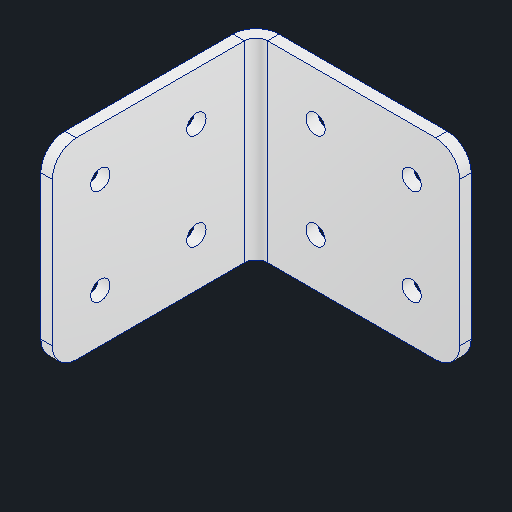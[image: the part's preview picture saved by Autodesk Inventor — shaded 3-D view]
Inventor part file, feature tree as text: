
AUTODESK INVENTOR PART (.ipt)
format: ipt  version: 2024.3 (Build 283343010, 343A)  size: 188,928 bytes
history: native  units: in
note: dims shown in document units (in); Inventor stores cm internally (conversion verified against a paired STEP export)
features: sheet_metal_op x4, sketch x4, hole x2, other x2, projected_geometry x2, chamfer x1
ambient origin geometry x8: Origin, YZ Plane, XZ Plane, XY Plane, X Axis, Y Axis, Z Axis, Center Point
bodies: Solid1 (feature_tree)
feature tree (15):
  sheet_metal_op  "Face1"
  sheet_metal_op  "Flange1"
  hole  "Hole1"  [1 undecoded]
  hole  "Hole2"  [1 undecoded]
  chamfer  "Corner Round1"
  sketch  "Sketch1"  dims[d0=2.0in d1=2.0in]
  other  "Plate1"
  sketch  "Sketch2"  dims[d2=0.12in d3=0.12in]
  other  "Plate2"
  sheet_metal_op  "Bend1"
  sheet_metal_op  "Corner1"
  sketch  "Sketch3"  dims[d4=0.06in]
  projected_geometry  "Projected Loop1"
  sketch  "Sketch4"  dims[d5=0.24in d6=0.12in d7=2.24in d8=90.0deg d9=0.12in d10=0.48in d11=0.12in d12=0.12in d13=0.5in d14=0.5in d15=0.7874in d17=1.0in d18=0.7874in d20=1.0in d23=0.201in d24=0.75in d25=0.385in d26=0.25in d27=0.5635in d28=0.12in d29=0.8108in d30=0.5in d31=0.5in d32=0.7874in d34=1.0in d35=0.7874in d37=1.0in d40=0.201in d41=0.75in d42=0.375in d43=0.25in d44=0.5635in d45=1.0in d46=0.8108in d47=0.25in d48=0.8108in d49=0.0625in d50=0.75in d51=0.375in]
  projected_geometry  "Projected Loop2"
note: 2 required parameter values undecoded (feature->parameter linkage not recoverable at this tier; creation-order binding heuristic only, values carry confidence <= 0.55)
